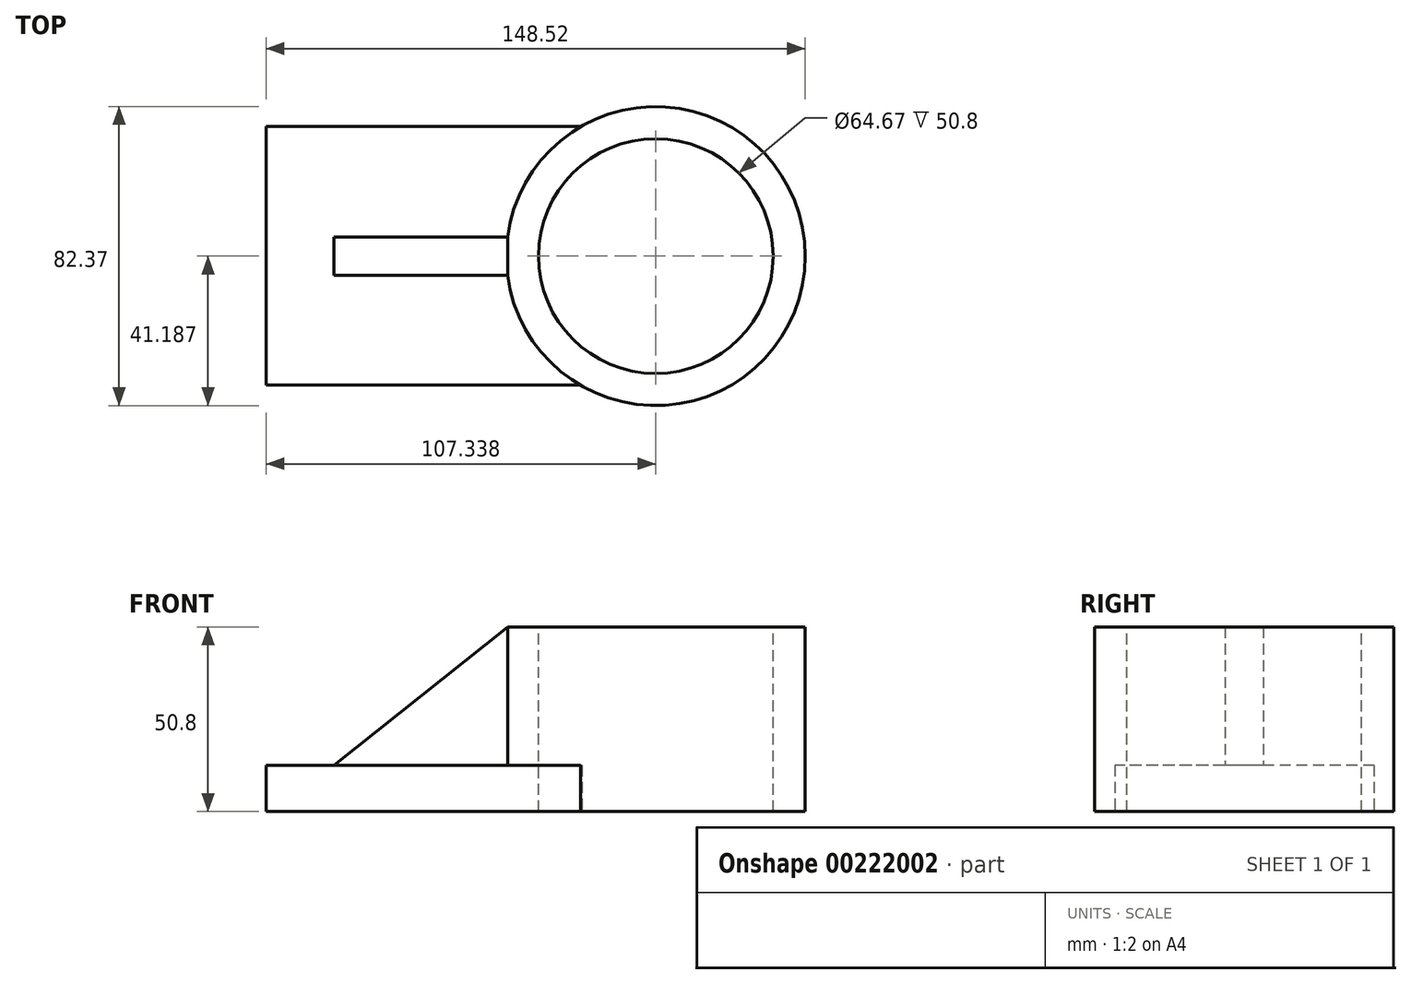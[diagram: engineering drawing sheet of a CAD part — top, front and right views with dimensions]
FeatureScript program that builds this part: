
annotation { "Feature Type Name" : "Feature", "Feature Type Description" : "" }
export const myFeature = defineFeature(function(context is Context, id is Id, definition is map)
    precondition{}
    {
        {
            var Q0;
            Q0=qCreatedBy(makeId("Top.planeOp"),FACE);
            var sketch = newSketch(context, id + "F0", { "sketchPlane" : qUnion([Q0])});
            skLineSegment(sketch, "E0.bottom", {"start": v(-56.8, 33.83) * mm, "end": v(37.87, 33.83) * mm});
            skLineSegment(sketch, "E0.top", {"start": v(-56.8, -37.52) * mm, "end": v(37.87, -37.52) * mm});
            skLineSegment(sketch, "E0.left", {"start": v(-56.8, 33.83) * mm, "end": v(-56.8, -37.52) * mm});
            skLineSegment(sketch, "E0.right", {"start": v(37.87, 33.83) * mm, "end": v(37.87, -37.52) * mm});
            skSolve(sketch);
        }
        {
            var Q0;
            Q0=makeQuery(id+"F0.imprint","IMPRINT",FACE,{"disambiguationData":[TD([[makeQuery(id+"F0.imprint","IMPRINT",EDGE,{"derivedFrom":sQuery(id+"F0.wireOp",EDGE,"E0.bottom")}),-1.0]])]});
            extrude(context, id + "F1", {"entities" : qUnion([Q0]), "depth" : 12.7 * mm});
        }
        {
            var Q0;
            Q0=makeQuery(id+"F1.opExtrude","CAP_FACE",FACE,{"disambiguationData":[OSD([sQuery(id+"F0.wireOp",EDGE,"E0.bottom"),sQuery(id+"F0.wireOp",EDGE,"E0.top"),sQuery(id+"F0.wireOp",EDGE,"E0.left"),sQuery(id+"F0.wireOp",EDGE,"E0.right")])],"isStart":false});
            var sketch = newSketch(context, id + "F2", { "sketchPlane" : qUnion([Q0])});
            skArc(sketch, "E1", {"start": v(37.87, 33.83) * mm, "mid": v(16.34, -1.85) * mm, "end": v(37.87, -37.52) * mm});
            skLineSegment(sketch, "E2", {"start": v(37.87, 33.83) * mm, "end": v(37.87, -37.52) * mm});
            skSolve(sketch);
        }
        {
            var Q0;
            Q0 = qSketchRegion(id + "F2", true);
            extrude(context, id + "F3", {"entities" : qUnion([Q0]), "operationType" : NewBodyOperationType.REMOVE, "endBound" : BoundingType.THROUGH_ALL, "oppositeDirection" : true, "depth" : 25.4 * mm});
        }
        {
            var Q0;
            Q0=qCreatedBy(makeId("Top.planeOp"),FACE);
            var sketch = newSketch(context, id + "F4", { "sketchPlane" : qUnion([Q0])});
            skCircle(sketch, "E3", {"center": v(50.54, -1.96) * mm, "radius": 41.18 * mm});
            skSolve(sketch);
        }
        {
            var Q0;
            Q0 = qSketchRegion(id + "F4", true);
            extrude(context, id + "F5", {"entities" : qUnion([Q0]), "operationType" : NewBodyOperationType.ADD, "depth" : 50.8 * mm});
        }
        {
            var Q0;
            Q0=makeQuery(id+"F5.opExtrude","CAP_FACE",FACE,{"disambiguationData":[OSD([sQuery(id+"F4.wireOp",EDGE,"E3")])],"isStart":false});
            var sketch = newSketch(context, id + "F6", { "sketchPlane" : qUnion([Q0])});
            skCircle(sketch, "E4", {"center": v(50.54, -1.96) * mm, "radius": 32.33 * mm});
            skSolve(sketch);
        }
        {
            var Q0;
            Q0 = qSketchRegion(id + "F6", true);
            extrude(context, id + "F7", {"entities" : qUnion([Q0]), "operationType" : NewBodyOperationType.REMOVE, "endBound" : BoundingType.THROUGH_ALL, "oppositeDirection" : true, "depth" : 25.4 * mm});
        }
        {
            var Q0;
            Q0=makeQuery(id+"F1.opExtrude","CAP_FACE",FACE,{"disambiguationData":[OSD([sQuery(id+"F0.wireOp",EDGE,"E0.bottom"),sQuery(id+"F0.wireOp",EDGE,"E0.top"),sQuery(id+"F0.wireOp",EDGE,"E0.left"),sQuery(id+"F0.wireOp",EDGE,"E0.right")])],"isStart":false});
            var sketch = newSketch(context, id + "F8", { "sketchPlane" : qUnion([Q0])});
            skLineSegment(sketch, "E5.bottom", {"start": v(9.7, 3.29) * mm, "end": v(-38.18, 3.29) * mm});
            skLineSegment(sketch, "E5.top", {"start": v(9.7, -7.26) * mm, "end": v(-38.18, -7.26) * mm});
            skLineSegment(sketch, "E5.left", {"start": v(9.7, 3.29) * mm, "end": v(9.7, -7.26) * mm});
            skLineSegment(sketch, "E5.right", {"start": v(-38.18, 3.29) * mm, "end": v(-38.18, -7.26) * mm});
            skSolve(sketch);
        }
        {
            var Q0;
            Q0 = qSketchRegion(id + "F8", true);
            extrude(context, id + "F9", {"entities" : qUnion([Q0]), "operationType" : NewBodyOperationType.ADD, "depth" : 38.1 * mm});
        }
        {
            var Q0;
            Q0=makeQuery(id+"F9.opExtrude","SWEPT_FACE",FACE,{"disambiguationData":[OSD([sQuery(id+"F8.wireOp",EDGE,"E5.top")])]});
            var sketch = newSketch(context, id + "F10", { "sketchPlane" : qUnion([Q0])});
            skLineSegment(sketch, "E6", {"start": v(9.7, 50.8) * mm, "end": v(-38.18, 12.7) * mm});
            skLineSegment(sketch, "E7", {"start": v(-38.18, 12.7) * mm, "end": v(-38.18, 50.8) * mm});
            skLineSegment(sketch, "E8", {"start": v(-38.18, 50.8) * mm, "end": v(9.7, 50.8) * mm});
            skSolve(sketch);
        }
        {
            var Q0;
            Q0 = qSketchRegion(id + "F10", true);
            extrude(context, id + "F11", {"entities" : qUnion([Q0]), "operationType" : NewBodyOperationType.REMOVE, "endBound" : BoundingType.THROUGH_ALL, "oppositeDirection" : true, "depth" : 25.4 * mm});
        }
    });
